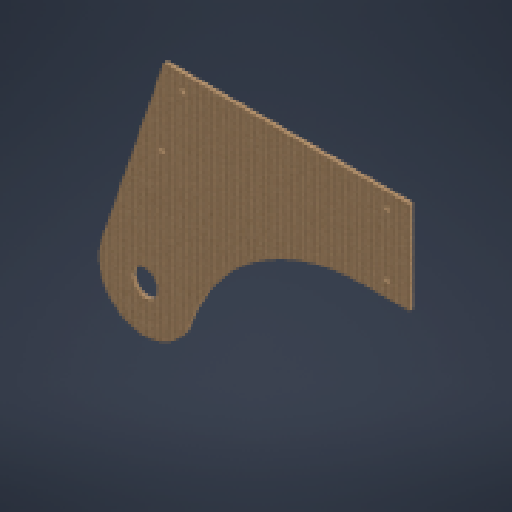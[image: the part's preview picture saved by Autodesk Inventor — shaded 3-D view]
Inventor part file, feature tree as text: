
AUTODESK INVENTOR PART (.ipt)
format: ipt  version: 2024.1 (Build 281209000, 209)  size: 204,288 bytes
history: native  units: in
note: dims shown in document units (in); Inventor stores cm internally (conversion verified against a paired STEP export)
features: other x5, sketch x4, extrude x3, projected_geometry x2, fillet x1, plane x1, reference x1
ambient origin geometry x8: Origin, YZ Plane, XZ Plane, XY Plane, X Axis, Y Axis, Z Axis, Center Point
bodies: Solid1 (feature_tree)
feature tree (17):
  extrude  "Extrusion1"  Depth=0.125in
  fillet  "Fillet1"  Radius=0.125in
  plane  "Work Plane1"
  sketch  "Sketch2"  dims[d4=6.0in d5=-0.1031in]
  sketch  "Sketch3"  dims[d6=0.84in d7=0.267in d8=0.0in]
  extrude  "Extrusion2"  [1 undecoded]
  extrude  "Extrusion3"  Depth=0.267in TaperAngle=0.0deg
  sketch  "Sketch1"  dims[d0=0.84in d1=10.0in d2=0.125in d3=0.0in]
  reference  "Reference1"
  other  "Work Point1"
  other  "Work Axis1"
  sketch  "Sketch4"  dims[d9=0.0in d10=0.0in]
  projected_geometry  "Projected Loop1"
  projected_geometry  "Projected Loop2"
  other  "<userpath>\Documents\School\FallCAD\Trebuchet\Trebuchet.iam"
  other  "Trebuchet.iam"
  other  "FrameTop:1"
note: 1 required parameter value undecoded (feature->parameter linkage not recoverable at this tier; creation-order binding heuristic only, values carry confidence <= 0.55)
